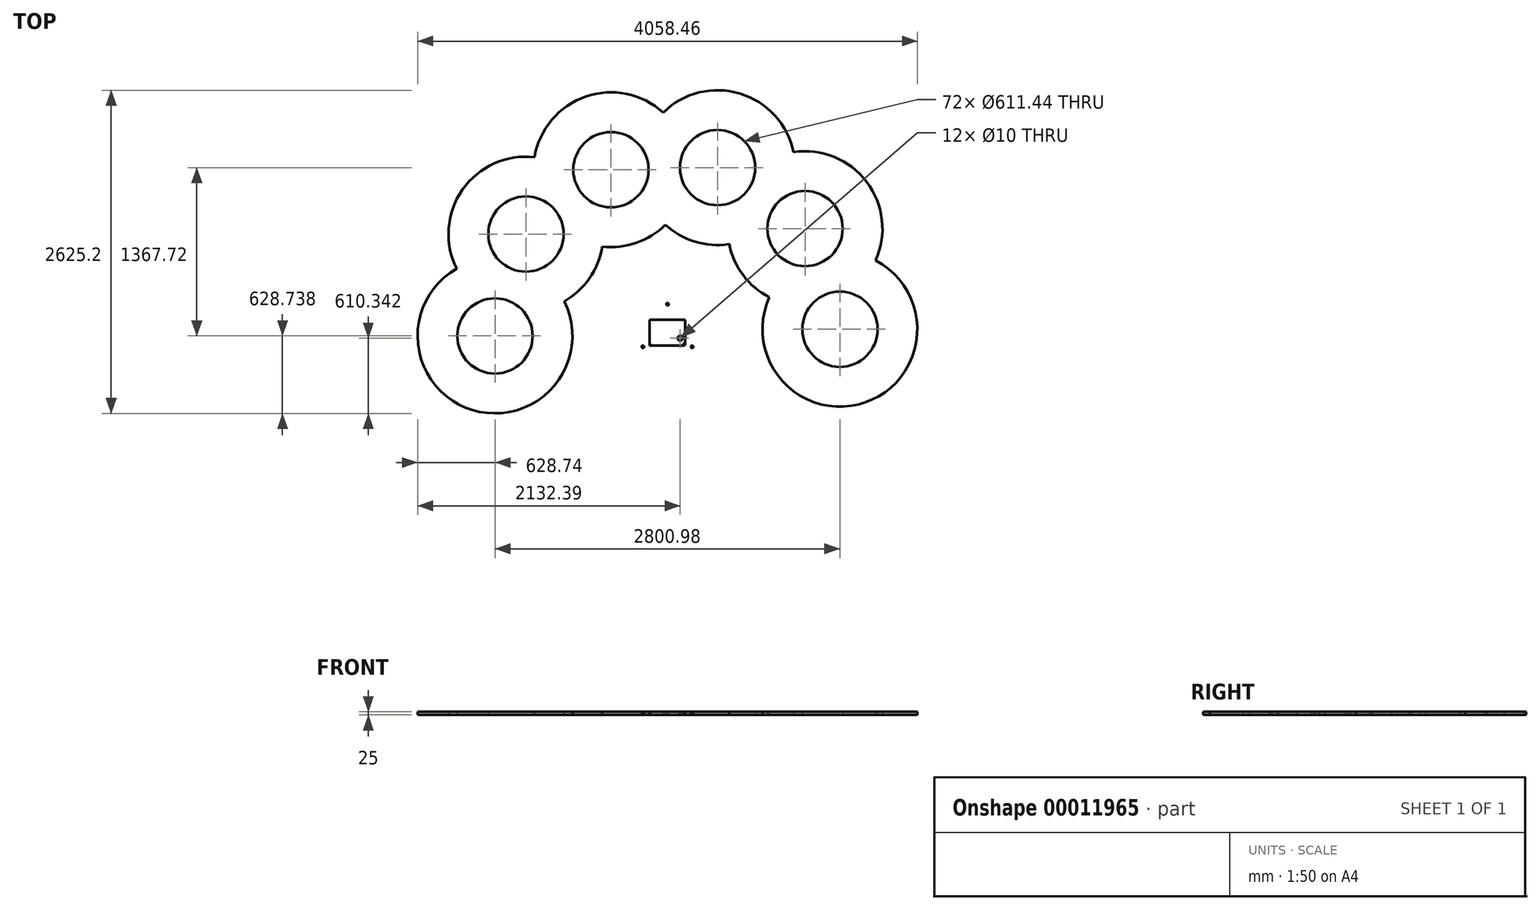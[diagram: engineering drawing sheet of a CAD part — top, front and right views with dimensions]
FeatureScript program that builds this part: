
annotation { "Feature Type Name" : "Feature", "Feature Type Description" : "" }
export const myFeature = defineFeature(function(context is Context, id is Id, definition is map)
    precondition{}
    {
        {
            var Q0;
            Q0=qCreatedBy(makeId("Top.planeOp"),FACE);
            var sketch = newSketch(context, id + "F0", { "sketchPlane" : qUnion([Q0])});
            skLineSegment(sketch, "E0.rect.bottom", {"start": v(144.53, 104.66) * mm, "end": v(-144.53, 104.66) * mm});
            skLineSegment(sketch, "E0.rect.top", {"start": v(144.53, -104.66) * mm, "end": v(-144.53, -104.66) * mm});
            skLineSegment(sketch, "E0.rect.left", {"start": v(144.53, 104.66) * mm, "end": v(144.53, -104.66) * mm});
            skLineSegment(sketch, "E0.rect.right", {"start": v(-144.53, 104.66) * mm, "end": v(-144.53, -104.66) * mm});
            skCircle(sketch, "E1", {"center": v(0, 230.94) * mm, "radius": 10 * mm});
            skCircle(sketch, "E2.1.0", {"center": v(-200, -115.47) * mm, "radius": 10 * mm});
            skCircle(sketch, "E2.2.0", {"center": v(200, -115.47) * mm, "radius": 10 * mm});
            skPoint(sketch, "E2.center", {"position": v(0, 0) * mm});
            skCircle(sketch, "E3", {"center": v(-1400.5, -27.33) * mm, "radius": 628.74 * mm});
            skCircle(sketch, "E4", {"center": v(-1400.5, -27.33) * mm, "radius": 305.72 * mm});
            skCircle(sketch, "E5.1.0", {"center": v(-1149.09, 801.08) * mm, "radius": 628.74 * mm});
            skCircle(sketch, "E5.1.1", {"center": v(-1149.09, 801.08) * mm, "radius": 305.72 * mm});
            skCircle(sketch, "E5.2.0", {"center": v(-458.77, 1323.5) * mm, "radius": 628.74 * mm});
            skCircle(sketch, "E5.2.1", {"center": v(-458.77, 1323.5) * mm, "radius": 305.72 * mm});
            skLineSegment(sketch, "E5.anchor1", {"start": v(0, 0) * mm, "end": v(-1400.5, -27.33) * mm, "construction": true});
            skLineSegment(sketch, "E5.anchor2", {"start": v(0, 0) * mm, "end": v(1400.5, 27.33) * mm, "construction": true});
            skCircle(sketch, "E6.1.3.0", {"center": v(406.78, 1340.4) * mm, "radius": 628.74 * mm});
            skCircle(sketch, "E6.2.3.0", {"center": v(406.78, 1340.4) * mm, "radius": 305.72 * mm});
            skCircle(sketch, "E6.1.4.0", {"center": v(1116.95, 845.3) * mm, "radius": 628.74 * mm});
            skCircle(sketch, "E6.2.4.0", {"center": v(1116.95, 845.3) * mm, "radius": 305.72 * mm});
            skCircle(sketch, "E6.1.5.0", {"center": v(1400.5, 27.33) * mm, "radius": 628.74 * mm});
            skCircle(sketch, "E6.2.5.0", {"center": v(1400.5, 27.33) * mm, "radius": 305.72 * mm});
            skSolve(sketch);
        }
        {
            var Q0;
            Q0 = qSketchRegion(id + "F0", true);
            extrude(context, id + "F1", {"entities" : qUnion([Q0]), "depth" : 25 * mm});
        }
        {
            var Q0;
            Q0=makeQuery(id+"F1.opExtrude","CAP_FACE",FACE,{"disambiguationData":[OSD([sQuery(id+"F0.wireOp",EDGE,"E0.rect.bottom"),sQuery(id+"F0.wireOp",EDGE,"E0.rect.top"),sQuery(id+"F0.wireOp",EDGE,"E0.rect.left"),sQuery(id+"F0.wireOp",EDGE,"E0.rect.right")])],"isStart":false});
            var sketch = newSketch(context, id + "F2", { "sketchPlane" : qUnion([Q0])});
            skPoint(sketch, "E7", {"position": v(-144.53, -104.66) * mm});
            skPoint(sketch, "E8", {"position": v(103.4, 18.39) * mm});
            skPoint(sketch, "E9", {"position": v(144.53, -104.66) * mm});
            skPoint(sketch, "E10", {"position": v(103.16, -45.73) * mm});
            skSolve(sketch);
        }
        {
            var Q0;
            Q0=sQuery(id+"F2.wireOp",VERTEX,"E7");
            var Q1;
            Q1=makeQuery(id+"F1.opExtrude","SWEPT_BODY",BODY,{"disambiguationData":[OSD([sQuery(id+"F0.wireOp",EDGE,"E0.rect.bottom"),sQuery(id+"F0.wireOp",EDGE,"E0.rect.top"),sQuery(id+"F0.wireOp",EDGE,"E0.rect.left"),sQuery(id+"F0.wireOp",EDGE,"E0.rect.right")])]});
            hole(context, id + "F3", {"style" : HoleStyle.SIMPLE, "holeDiameter" : 25 * mm, "endStyle" : HoleEndStyle.BLIND, "holeDepth" : 3 * mm, "locations" : qUnion([Q0]), "scope" : qUnion([Q1])});
        }
        {
            var Q0;
            Q0=sQuery(id+"F2.wireOp",VERTEX,"E9");
            var Q1;
            Q1=sQuery(id+"F2.wireOp",VERTEX,"E10");
            var Q2;
            Q2=makeQuery(id+"F1.opExtrude","SWEPT_BODY",BODY,{"disambiguationData":[OSD([sQuery(id+"F0.wireOp",EDGE,"E0.rect.bottom"),sQuery(id+"F0.wireOp",EDGE,"E0.rect.top"),sQuery(id+"F0.wireOp",EDGE,"E0.rect.left"),sQuery(id+"F0.wireOp",EDGE,"E0.rect.right")])]});
            hole(context, id + "F4", {"style" : HoleStyle.C_SINK, "holeDiameter" : 10 * mm, "cSinkDiameter" : 40 * mm, "endStyle" : HoleEndStyle.THROUGH, "locations" : qUnion([Q0, Q1]), "scope" : qUnion([Q2]), "cSinkAngle" : 90 * degree});
        }
        {
            var Q0;
            Q0=makeQuery(id+"F1.opExtrude","SWEPT_FACE",FACE,{"disambiguationData":[OSD([sQuery(id+"F0.wireOp",EDGE,"E0.rect.top")])]});
            var sketch = newSketch(context, id + "F5", { "sketchPlane" : qUnion([Q0])});
            skLineSegment(sketch, "E11.0", {"start": v(-144.53, 15.56) * mm, "end": v(-144.53, 0) * mm});
            skLineSegment(sketch, "E12.0", {"start": v(-132.03, 22) * mm, "end": v(-144.53, 15.56) * mm});
            skLineSegment(sketch, "E13.0.MirrorCS", {"start": v(-157.03, 22) * mm, "end": v(-144.53, 15.56) * mm});
            skLineSegment(sketch, "E14.0", {"start": v(137.77, 0) * mm, "end": v(137.77, 10.86) * mm, "construction": true});
            skLineSegment(sketch, "E14.1", {"start": v(137.77, 10.86) * mm, "end": v(127.77, 25) * mm});
            skLineSegment(sketch, "E15.0.MirrorCS", {"start": v(137.77, 10.86) * mm, "end": v(147.77, 25) * mm});
            skSolve(sketch);
        }
    });
